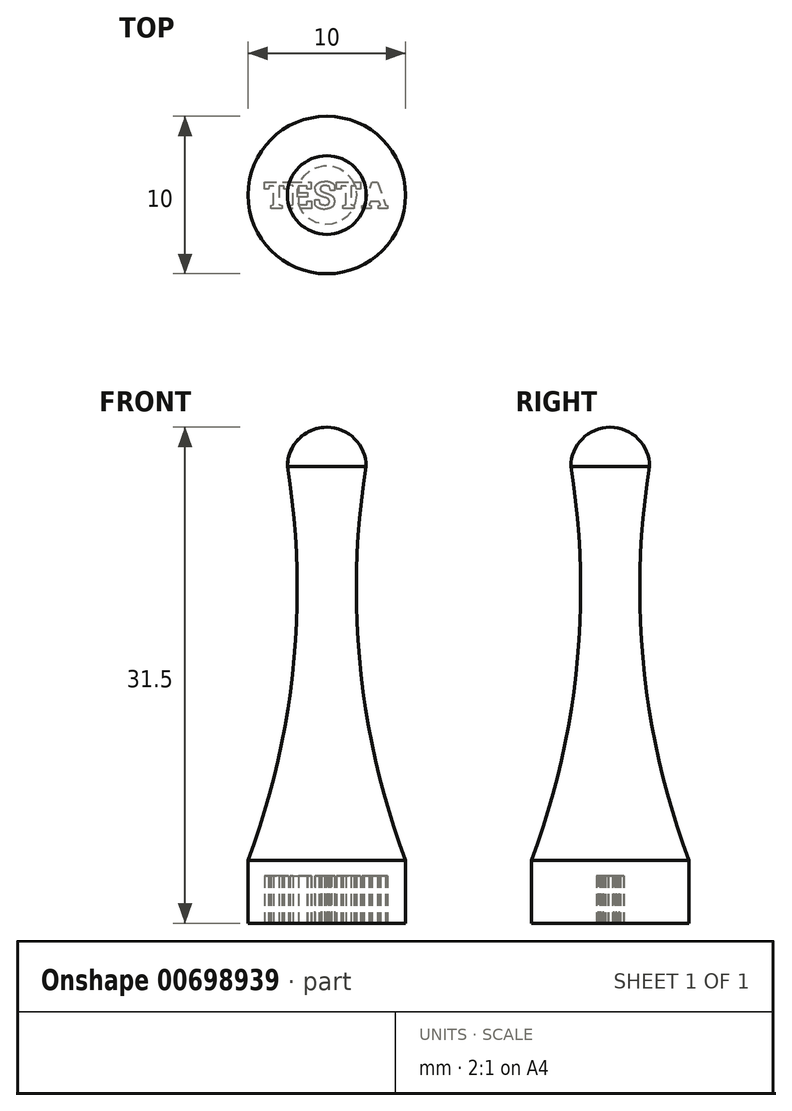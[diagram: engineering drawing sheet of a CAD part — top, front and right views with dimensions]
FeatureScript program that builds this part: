
annotation { "Feature Type Name" : "Feature", "Feature Type Description" : "" }
export const myFeature = defineFeature(function(context is Context, id is Id, definition is map)
    precondition{}
    {
        {
            var Q0;
            Q0=qCreatedBy(makeId("Top.planeOp"),FACE);
            var sketch = newSketch(context, id + "F0", { "sketchPlane" : qUnion([Q0])});
            skText(sketch, "E0", { "text": "TESTA", "fontName": "RobotoSlab-Bold.ttf"});
            skLineSegment(sketch, "E1", {"start": v(0, 0) * mm, "end": v(8, -1.72) * mm, "construction": true});
            skLineSegment(sketch, "E2", {"start": v(8, 0) * mm, "end": v(0, -1.72) * mm, "construction": true});
            skCircle(sketch, "E3", {"center": v(4, -0.86) * mm, "radius": 5 * mm});
            const initialGuessF0  = {"E0": [0, -0.00172, 1, 0, 0.00172]};
            skSetInitialGuess(sketch, initialGuessF0);
            skSolve(sketch);
        }
        {
            var Q0;
            Q0=makeQuery(id+"F0.imprint","IMPRINT",FACE,{"disambiguationData":[TD([[makeQuery(id+"F0.imprint","IMPRINT",EDGE,{"derivedFrom":sQuery(id+"F0.wireOp",EDGE,"E0.sketch_text.stroke-0")}),1.0]])]});
            extrude(context, id + "F1", {"entities" : qUnion([Q0]), "depth" : 3 * mm, "offsetDistance" : 25 * mm});
        }
        {
            var Q0;
            Q0=makeQuery(id+"F1.opExtrude","CAP_FACE",FACE,{"disambiguationData":[OSD([sQuery(id+"F0.wireOp",EDGE,"E0.sketch_text.stroke-0"),sQuery(id+"F0.wireOp",EDGE,"E0.sketch_text.stroke-1"),sQuery(id+"F0.wireOp",EDGE,"E0.sketch_text.stroke-2"),sQuery(id+"F0.wireOp",EDGE,"E0.sketch_text.stroke-3"),sQuery(id+"F0.wireOp",EDGE,"E0.sketch_text.stroke-4"),sQuery(id+"F0.wireOp",EDGE,"E0.sketch_text.stroke-5"),sQuery(id+"F0.wireOp",EDGE,"E0.sketch_text.stroke-6"),sQuery(id+"F0.wireOp",EDGE,"E0.sketch_text.stroke-7"),sQuery(id+"F0.wireOp",EDGE,"E0.sketch_text.stroke-8"),sQuery(id+"F0.wireOp",EDGE,"E0.sketch_text.stroke-9"),sQuery(id+"F0.wireOp",EDGE,"E0.sketch_text.stroke-10"),sQuery(id+"F0.wireOp",EDGE,"E0.sketch_text.stroke-11"),sQuery(id+"F0.wireOp",EDGE,"E0.sketch_text.stroke-12"),sQuery(id+"F0.wireOp",EDGE,"E0.sketch_text.stroke-13"),sQuery(id+"F0.wireOp",EDGE,"E0.sketch_text.stroke-14"),sQuery(id+"F0.wireOp",EDGE,"E0.sketch_text.stroke-15"),sQuery(id+"F0.wireOp",EDGE,"E0.sketch_text.stroke-16"),sQuery(id+"F0.wireOp",EDGE,"E0.sketch_text.stroke-17"),sQuery(id+"F0.wireOp",EDGE,"E0.sketch_text.stroke-18"),sQuery(id+"F0.wireOp",EDGE,"E0.sketch_text.stroke-19"),sQuery(id+"F0.wireOp",EDGE,"E0.sketch_text.stroke-20"),sQuery(id+"F0.wireOp",EDGE,"E0.sketch_text.stroke-21"),sQuery(id+"F0.wireOp",EDGE,"E0.sketch_text.stroke-22"),sQuery(id+"F0.wireOp",EDGE,"E0.sketch_text.stroke-23"),sQuery(id+"F0.wireOp",EDGE,"E0.sketch_text.stroke-24"),sQuery(id+"F0.wireOp",EDGE,"E0.sketch_text.stroke-25"),sQuery(id+"F0.wireOp",EDGE,"E0.sketch_text.stroke-26"),sQuery(id+"F0.wireOp",EDGE,"E0.sketch_text.stroke-27"),sQuery(id+"F0.wireOp",EDGE,"E0.sketch_text.stroke-28"),sQuery(id+"F0.wireOp",EDGE,"E0.sketch_text.stroke-29"),sQuery(id+"F0.wireOp",EDGE,"E0.sketch_text.stroke-30"),sQuery(id+"F0.wireOp",EDGE,"E0.sketch_text.stroke-31"),sQuery(id+"F0.wireOp",EDGE,"E0.sketch_text.stroke-32"),sQuery(id+"F0.wireOp",EDGE,"E0.sketch_text.stroke-33"),sQuery(id+"F0.wireOp",EDGE,"E0.sketch_text.stroke-34"),sQuery(id+"F0.wireOp",EDGE,"E0.sketch_text.stroke-35"),sQuery(id+"F0.wireOp",EDGE,"E0.sketch_text.stroke-36"),sQuery(id+"F0.wireOp",EDGE,"E0.sketch_text.stroke-37"),sQuery(id+"F0.wireOp",EDGE,"E0.sketch_text.stroke-38"),sQuery(id+"F0.wireOp",EDGE,"E0.sketch_text.stroke-39"),sQuery(id+"F0.wireOp",EDGE,"E0.sketch_text.stroke-40"),sQuery(id+"F0.wireOp",EDGE,"E0.sketch_text.stroke-41"),sQuery(id+"F0.wireOp",EDGE,"E0.sketch_text.stroke-42"),sQuery(id+"F0.wireOp",EDGE,"E0.sketch_text.stroke-43"),sQuery(id+"F0.wireOp",EDGE,"E0.sketch_text.stroke-44"),sQuery(id+"F0.wireOp",EDGE,"E0.sketch_text.stroke-45"),sQuery(id+"F0.wireOp",EDGE,"E0.sketch_text.stroke-46"),sQuery(id+"F0.wireOp",EDGE,"E0.sketch_text.stroke-47"),sQuery(id+"F0.wireOp",EDGE,"E0.sketch_text.stroke-48"),sQuery(id+"F0.wireOp",EDGE,"E0.sketch_text.stroke-49"),sQuery(id+"F0.wireOp",EDGE,"E0.sketch_text.stroke-50"),sQuery(id+"F0.wireOp",EDGE,"E0.sketch_text.stroke-51"),sQuery(id+"F0.wireOp",EDGE,"E0.sketch_text.stroke-52"),sQuery(id+"F0.wireOp",EDGE,"E0.sketch_text.stroke-53"),sQuery(id+"F0.wireOp",EDGE,"E0.sketch_text.stroke-54"),sQuery(id+"F0.wireOp",EDGE,"E0.sketch_text.stroke-55"),sQuery(id+"F0.wireOp",EDGE,"E0.sketch_text.stroke-56"),sQuery(id+"F0.wireOp",EDGE,"E0.sketch_text.stroke-57"),sQuery(id+"F0.wireOp",EDGE,"E0.sketch_text.stroke-58"),sQuery(id+"F0.wireOp",EDGE,"E0.sketch_text.stroke-59"),sQuery(id+"F0.wireOp",EDGE,"E0.sketch_text.stroke-60"),sQuery(id+"F0.wireOp",EDGE,"E0.sketch_text.stroke-61"),sQuery(id+"F0.wireOp",EDGE,"E0.sketch_text.stroke-62"),sQuery(id+"F0.wireOp",EDGE,"E0.sketch_text.stroke-63"),sQuery(id+"F0.wireOp",EDGE,"E0.sketch_text.stroke-64"),sQuery(id+"F0.wireOp",EDGE,"E0.sketch_text.stroke-65"),sQuery(id+"F0.wireOp",EDGE,"E0.sketch_text.stroke-66"),sQuery(id+"F0.wireOp",EDGE,"E0.sketch_text.stroke-67"),sQuery(id+"F0.wireOp",EDGE,"E0.sketch_text.stroke-68"),sQuery(id+"F0.wireOp",EDGE,"E0.sketch_text.stroke-69"),sQuery(id+"F0.wireOp",EDGE,"E0.sketch_text.stroke-70"),sQuery(id+"F0.wireOp",EDGE,"E0.sketch_text.stroke-71"),sQuery(id+"F0.wireOp",EDGE,"E0.sketch_text.stroke-72"),sQuery(id+"F0.wireOp",EDGE,"E0.sketch_text.stroke-73"),sQuery(id+"F0.wireOp",EDGE,"E0.sketch_text.stroke-74"),sQuery(id+"F0.wireOp",EDGE,"E0.sketch_text.stroke-75"),sQuery(id+"F0.wireOp",EDGE,"E0.sketch_text.stroke-76"),sQuery(id+"F0.wireOp",EDGE,"E0.sketch_text.stroke-77"),sQuery(id+"F0.wireOp",EDGE,"E0.sketch_text.stroke-78"),sQuery(id+"F0.wireOp",EDGE,"E0.sketch_text.stroke-79"),sQuery(id+"F0.wireOp",EDGE,"E0.sketch_text.stroke-80"),sQuery(id+"F0.wireOp",EDGE,"E0.sketch_text.stroke-81"),sQuery(id+"F0.wireOp",EDGE,"E0.sketch_text.stroke-82"),sQuery(id+"F0.wireOp",EDGE,"E0.sketch_text.stroke-83"),sQuery(id+"F0.wireOp",EDGE,"E0.sketch_text.stroke-84"),sQuery(id+"F0.wireOp",EDGE,"E0.sketch_text.stroke-85"),sQuery(id+"F0.wireOp",EDGE,"E0.sketch_text.stroke-86"),sQuery(id+"F0.wireOp",EDGE,"E0.sketch_text.stroke-87"),sQuery(id+"F0.wireOp",EDGE,"E0.sketch_text.stroke-88"),sQuery(id+"F0.wireOp",EDGE,"E0.sketch_text.stroke-89"),sQuery(id+"F0.wireOp",EDGE,"E0.sketch_text.stroke-90"),sQuery(id+"F0.wireOp",EDGE,"E0.sketch_text.stroke-91"),sQuery(id+"F0.wireOp",EDGE,"E0.sketch_text.stroke-92"),sQuery(id+"F0.wireOp",EDGE,"E0.sketch_text.stroke-93"),sQuery(id+"F0.wireOp",EDGE,"E0.sketch_text.stroke-94"),sQuery(id+"F0.wireOp",EDGE,"E0.sketch_text.stroke-95"),sQuery(id+"F0.wireOp",EDGE,"E0.sketch_text.stroke-96"),sQuery(id+"F0.wireOp",EDGE,"E0.sketch_text.stroke-97"),sQuery(id+"F0.wireOp",EDGE,"E0.sketch_text.stroke-98"),sQuery(id+"F0.wireOp",EDGE,"E3")])],"isStart":false});
            var sketch = newSketch(context, id + "F2", { "sketchPlane" : qUnion([Q0])});
            skCircle(sketch, "E4", {"center": v(4, -0.86) * mm, "radius": 5 * mm});
            skPoint(sketch, "E4.first.point", {"position": v(1, 3.14) * mm});
            skPoint(sketch, "E4.second.point", {"position": v(8.8, 0.54) * mm});
            skPoint(sketch, "E4.third.point", {"position": v(2.36, -5.58) * mm});
            skSolve(sketch);
        }
        {
            var Q0;
            Q0=makeQuery(id+"F2.imprint","IMPRINT",FACE,{"disambiguationData":[TD([[makeQuery(id+"F2.imprint","IMPRINT",EDGE,{"derivedFrom":makeQuery(id+"F1.opExtrude","CAP_EDGE",EDGE,{"disambiguationData":[OSD([sQuery(id+"F0.wireOp",EDGE,"E0.sketch_text.stroke-0")])],"isStart":false})}),-1.0]])]});
            var Q1;
            Q1=makeQuery(id+"F2.imprint","IMPRINT",FACE,{"disambiguationData":[TD([[makeQuery(id+"F2.imprint","IMPRINT",EDGE,{"derivedFrom":makeQuery(id+"F1.opExtrude","CAP_EDGE",EDGE,{"disambiguationData":[OSD([sQuery(id+"F0.wireOp",EDGE,"E0.sketch_text.stroke-16")])],"isStart":false})}),-1.0]])]});
            var Q2;
            Q2=makeQuery(id+"F2.imprint","IMPRINT",FACE,{"disambiguationData":[TD([[makeQuery(id+"F2.imprint","IMPRINT",EDGE,{"derivedFrom":makeQuery(id+"F1.opExtrude","CAP_EDGE",EDGE,{"disambiguationData":[OSD([sQuery(id+"F0.wireOp",EDGE,"E0.sketch_text.stroke-37")])],"isStart":false})}),-1.0]])]});
            var Q3;
            Q3=makeQuery(id+"F2.imprint","IMPRINT",FACE,{"disambiguationData":[TD([[makeQuery(id+"F2.imprint","IMPRINT",EDGE,{"derivedFrom":makeQuery(id+"F1.opExtrude","CAP_EDGE",EDGE,{"disambiguationData":[OSD([sQuery(id+"F0.wireOp",EDGE,"E0.sketch_text.stroke-67")])],"isStart":false})}),-1.0]])]});
            var Q4;
            Q4=makeQuery(id+"F2.imprint","IMPRINT",FACE,{"disambiguationData":[TD([[makeQuery(id+"F2.imprint","IMPRINT",EDGE,{"derivedFrom":makeQuery(id+"F1.opExtrude","CAP_EDGE",EDGE,{"disambiguationData":[OSD([sQuery(id+"F0.wireOp",EDGE,"E0.sketch_text.stroke-83")])],"isStart":false})}),-1.0]])]});
            var Q5;
            Q5=makeQuery(id+"F2.imprint","IMPRINT",FACE,{"disambiguationData":[TD([[makeQuery(id+"F2.imprint","IMPRINT",EDGE,{"derivedFrom":sQuery(id+"F2.wireOp",EDGE,"E4")}),1.0]])]});
            extrude(context, id + "F3", {"entities" : qUnion([Q0, Q1, Q2, Q3, Q4, Q5]), "operationType" : NewBodyOperationType.ADD, "depth" : 1 * mm, "offsetDistance" : 25 * mm});
        }
        {
            var Q0;
            Q0=makeQuery(id+"F3.opExtrude","CAP_FACE",FACE,{"disambiguationData":[OSD([sQuery(id+"F2.wireOp",EDGE,"E4")])],"isStart":false});
            var sketch = newSketch(context, id + "F4", { "sketchPlane" : qUnion([Q0])});
            skCircle(sketch, "E5", {"center": v(4, -0.86) * mm, "radius": 5 * mm});
            skPoint(sketch, "E5.first.point", {"position": v(1.95, 3.7) * mm});
            skPoint(sketch, "E5.second.point", {"position": v(8.4, -3.24) * mm});
            skPoint(sketch, "E5.third.point", {"position": v(1.35, -5.1) * mm});
            skLineSegment(sketch, "E6.bottom", {"start": v(4, -0.86) * mm, "end": v(14, -0.86) * mm});
            skLineSegment(sketch, "E6.top", {"start": v(4, -1.06) * mm, "end": v(14, -1.06) * mm});
            skLineSegment(sketch, "E6.left", {"start": v(4, -0.86) * mm, "end": v(4, -1.06) * mm});
            skLineSegment(sketch, "E6.right", {"start": v(14, -0.86) * mm, "end": v(14, -1.06) * mm});
            skSolve(sketch);
        }
        {
            var Q0;
            {var subQ5=sQuery(id+"F4.wireOp",EDGE,"E6.left");Q0=makeQuery(id+"F4.imprint","IMPRINT",FACE,{"disambiguationData":[TD([[makeQuery(id+"F4.imprint","IMPRINT",EDGE,{"derivedFrom":subQ5}),1.0]])]});}
            extrude(context, id + "F5", {"entities" : qUnion([Q0]), "operationType" : NewBodyOperationType.ADD, "depth" : 25 * mm, "offsetDistance" : 25 * mm});
        }
        {
            var Q0;
            Q0=makeQuery(id+"F5.opExtrude","SWEPT_FACE",FACE,{"disambiguationData":[OSD([sQuery(id+"F4.wireOp",EDGE,"E6.bottom")])]});
            var sketch = newSketch(context, id + "F6", { "sketchPlane" : qUnion([Q0])});
            skCircle(sketch, "E7", {"center": v(-4, 4) * mm, "radius": 5 * mm});
            skCircle(sketch, "E8", {"center": v(-4, 29) * mm, "radius": 2.5 * mm});
            skLineSegment(sketch, "E9", {"start": v(-4, 26.5) * mm, "end": v(-4, 9) * mm});
            skLineSegment(sketch, "E10", {"start": v(-4, 17.75) * mm, "end": v(-6, 17.75) * mm});
            skArc(sketch, "E11", {"start": v(-9, 4) * mm, "mid": v(-6.12, 16.34) * mm, "end": v(-6.5, 29) * mm});
            skLineSegment(sketch, "E12", {"start": v(-4, 29) * mm, "end": v(-4, 31.5) * mm});
            skLineSegment(sketch, "E13", {"start": v(-4, 9) * mm, "end": v(-4, 4) * mm});
            skLineSegment(sketch, "E14", {"start": v(-4, 4) * mm, "end": v(-9, 4) * mm});
            skSolve(sketch);
        }
        {
            var Q0;
            {var subQ4=sQuery(id+"F6.wireOp",EDGE,"E12");Q0=makeQuery(id+"F6.imprint","IMPRINT",FACE,{"disambiguationData":[TD([[makeQuery(id+"F6.imprint","IMPRINT",EDGE,{"derivedFrom":subQ4}),1.0]])]});}
            var Q1;
            {var subQ0=sQuery(id+"F6.wireOp",EDGE,"E8");var subQ4=sQuery(id+"F6.wireOp",EDGE,"E11");var subQ5=makeQuery(id+"F6.imprint","INTERSECT",VERTEX,{"derivedFrom":[subQ0,subQ4]});Q1=makeQuery(id+"F6.imprint","IMPRINT",FACE,{"disambiguationData":[TD([[makeQuery(id+"F6.imprint","IMPRINT",EDGE,{"disambiguationData":[TD([[subQ5,-1.0]])],"derivedFrom":subQ4}),-1.0]])]});}
            var Q2;
            {var subQ5=sQuery(id+"F6.wireOp",EDGE,"E10");Q2=makeQuery(id+"F6.imprint","IMPRINT",FACE,{"disambiguationData":[TD([[makeQuery(id+"F6.imprint","IMPRINT",EDGE,{"derivedFrom":subQ5}),-1.0]])]});}
            var Q3;
            {var subQ5=sQuery(id+"F6.wireOp",EDGE,"E10");Q3=makeQuery(id+"F6.imprint","IMPRINT",FACE,{"disambiguationData":[TD([[makeQuery(id+"F6.imprint","IMPRINT",EDGE,{"derivedFrom":subQ5}),1.0]])]});}
            var Q4;
            {var subQ0=sQuery(id+"F6.wireOp",EDGE,"E13");Q4=makeQuery(id+"F6.imprint","IMPRINT",FACE,{"disambiguationData":[TD([[makeQuery(id+"F6.imprint","IMPRINT",EDGE,{"derivedFrom":subQ0}),-1.0]])]});}
            var Q5;
            Q5=sQuery(id+"F6.wireOp",EDGE,"E9");
            revolve(context, id + "F7", {"operationType" : NewBodyOperationType.ADD, "entities" : qUnion([Q0, Q1, Q2, Q3, Q4]), "axis" : qUnion([Q5]), "revolveType" : RevolveType.FULL});
        }
        {
            var Q0;
            Q0=makeQuery(id+"F5.opExtrude","SWEPT_FACE",FACE,{"disambiguationData":[OSD([sQuery(id+"F4.wireOp",EDGE,"E6.bottom")])]});
            var Q1;
            Q1=makeQuery(id+"F7.opRevolve","SWEPT_FACE",FACE,{"disambiguationData":[OSD([sQuery(id+"F6.wireOp",EDGE,"E11")])]});
            revolve(context, id + "F8", {"operationType" : NewBodyOperationType.REMOVE, "entities" : qUnion([Q0]), "axis" : qUnion([Q1]), "revolveType" : RevolveType.FULL, "oppositeDirection" : true});
        }
    });
